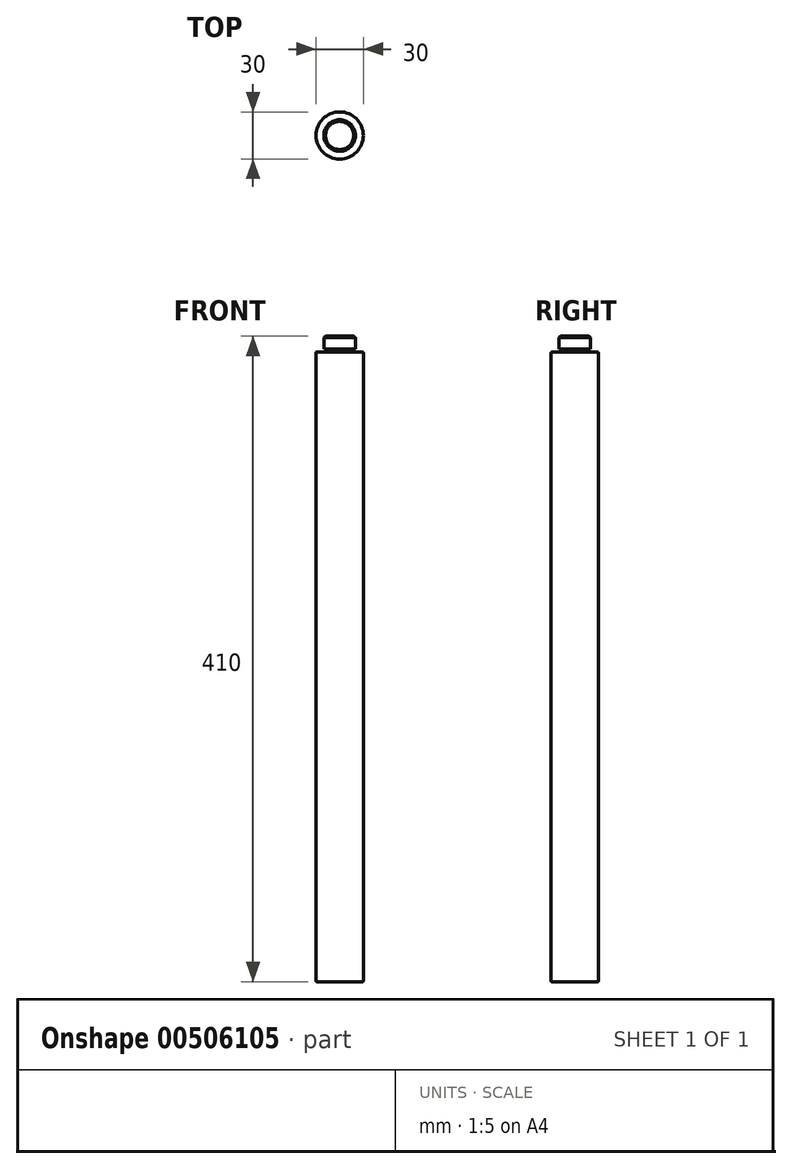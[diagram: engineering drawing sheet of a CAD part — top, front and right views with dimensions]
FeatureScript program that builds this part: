
annotation { "Feature Type Name" : "Feature", "Feature Type Description" : "" }
export const myFeature = defineFeature(function(context is Context, id is Id, definition is map)
    precondition{}
    {
        {
            var Q0;
            Q0=qCreatedBy(makeId("Top.planeOp"),FACE);
            var sketch = newSketch(context, id + "F0", { "sketchPlane" : qUnion([Q0])});
            skCircle(sketch, "E0", {"center": v(0, 0) * mm, "radius": 15 * mm});
            skSolve(sketch);
        }
        {
            var Q0;
            Q0 = qSketchRegion(id + "F0", true);
            extrude(context, id + "F1", {"entities" : qUnion([Q0]), "oppositeDirection" : true, "depth" : 400 * mm});
        }
        {
            var Q0;
            Q0=makeQuery(id+"F1.opExtrude","CAP_FACE",FACE,{"disambiguationData":[OSD([sQuery(id+"F0.wireOp",EDGE,"E0")])],"isStart":true});
            var sketch = newSketch(context, id + "F2", { "sketchPlane" : qUnion([Q0])});
            skCircle(sketch, "E1", {"center": v(0, 0) * mm, "radius": 10 * mm});
            skSolve(sketch);
        }
        {
            var Q0;
            Q0 = qSketchRegion(id + "F2", true);
            extrude(context, id + "F3", {"entities" : qUnion([Q0]), "operationType" : NewBodyOperationType.ADD, "depth" : 10 * mm});
        }
        {
            var Q0;
            Q0=makeQuery(id+"F1.opExtrude","CAP_EDGE",EDGE,{"disambiguationData":[OSD([sQuery(id+"F0.wireOp",EDGE,"E0")])],"isStart":false});
            var Q1;
            Q1=makeQuery(id+"F1.opExtrude","CAP_EDGE",EDGE,{"disambiguationData":[OSD([sQuery(id+"F0.wireOp",EDGE,"E0")])],"isStart":true});
            fillet(context, id + "F4", {"entities" : qUnion([Q0, Q1]), "radius" : 0.5 * mm, "tangentPropagation" : true, "allowEdgeOverflow" : false});
        }
        {
            var Q0;
            Q0=makeQuery(id+"F3.opExtrude","CAP_EDGE",EDGE,{"disambiguationData":[OSD([sQuery(id+"F2.wireOp",EDGE,"E1")])],"isStart":false});
            chamfer(context, id + "F5", {"entities" : qUnion([Q0]), "width" : 1 * mm, "tangentPropagation" : true});
        }
        {
            var Q0;
            Q0=qCreatedBy(makeId("Front.planeOp"),FACE);
            var sketch = newSketch(context, id + "F6", { "sketchPlane" : qUnion([Q0])});
            skLineSegment(sketch, "E2", {"start": v(0, 0) * mm, "end": v(0, 24.11) * mm, "construction": true});
            skLineSegment(sketch, "E3", {"start": v(-10, 0) * mm, "end": v(-10, 2) * mm});
            skLineSegment(sketch, "E4", {"start": v(-10, 0) * mm, "end": v(-9, 0) * mm});
            skLineSegment(sketch, "E5", {"start": v(-9, 0) * mm, "end": v(-9, 2) * mm});
            skLineSegment(sketch, "E6", {"start": v(-10, 2) * mm, "end": v(-9, 2) * mm});
            skPoint(sketch, "E7.orphan", {"position": v(-10, 9) * mm});
            skSolve(sketch);
        }
        {
            var Q0;
            Q0 = qSketchRegion(id + "F6", true);
            var Q1;
            Q1=sQuery(id+"F6.wireOp",EDGE,"E2");
            revolve(context, id + "F7", {"operationType" : NewBodyOperationType.REMOVE, "entities" : qUnion([Q0]), "axis" : qUnion([Q1]), "revolveType" : RevolveType.FULL, "oppositeDirection" : true});
        }
    });
